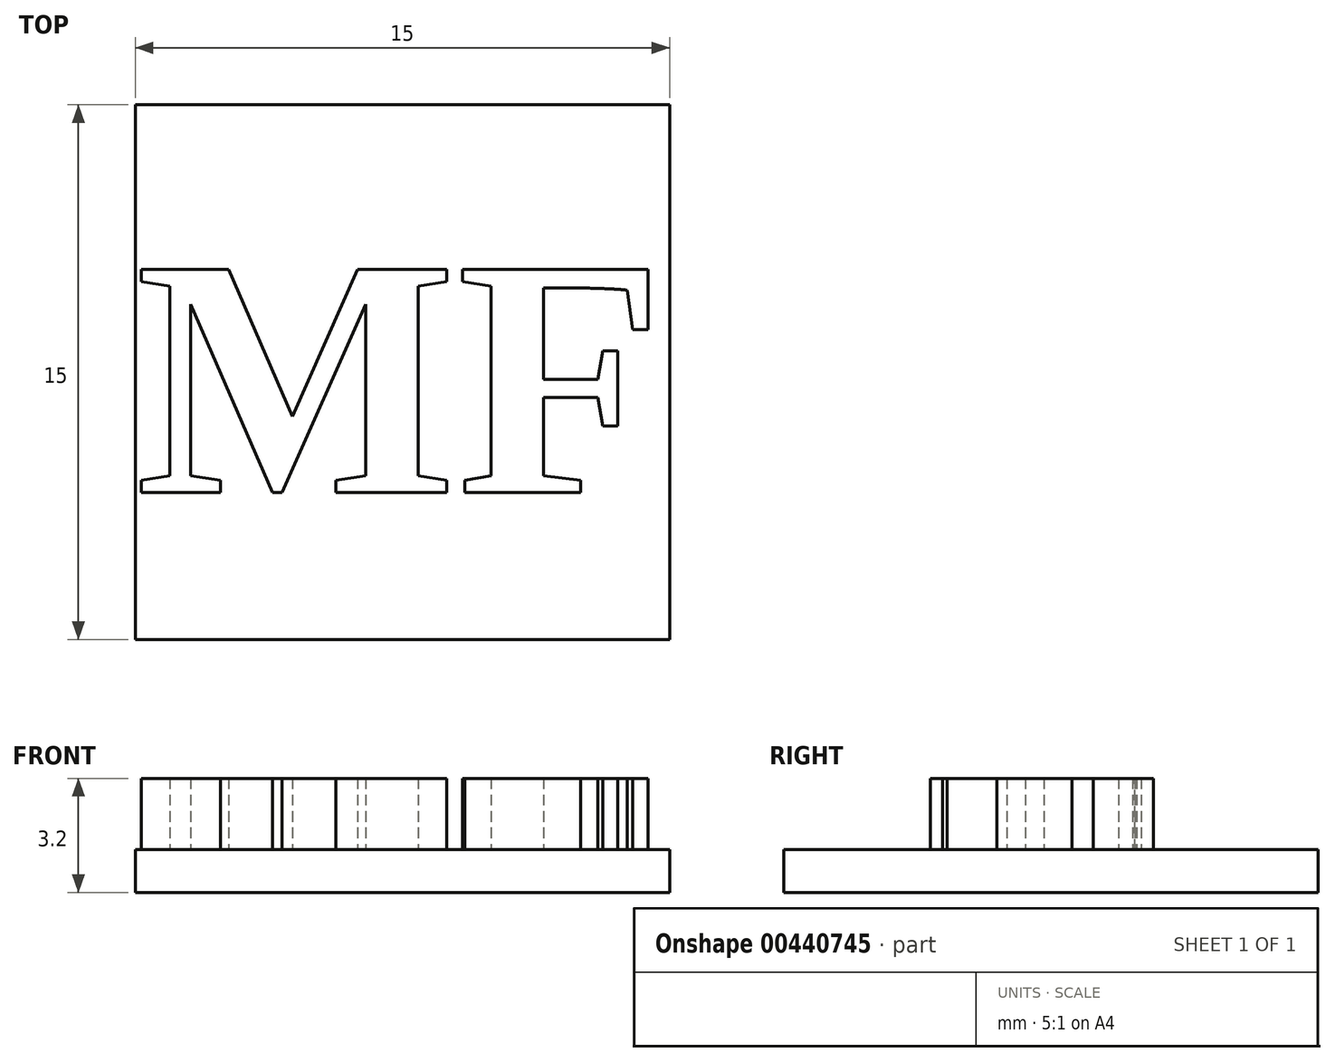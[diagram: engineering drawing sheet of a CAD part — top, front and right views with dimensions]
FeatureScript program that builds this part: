
annotation { "Feature Type Name" : "Feature", "Feature Type Description" : "" }
export const myFeature = defineFeature(function(context is Context, id is Id, definition is map)
    precondition{}
    {
        {
            var Q0;
            Q0=qCreatedBy(makeId("Top.planeOp"),FACE);
            var sketch = newSketch(context, id + "F0", { "sketchPlane" : qUnion([Q0])});
            skLineSegment(sketch, "E0.bottom", {"start": v(0, 0) * mm, "end": v(15, 0) * mm});
            skLineSegment(sketch, "E0.top", {"start": v(0, 15) * mm, "end": v(15, 15) * mm});
            skLineSegment(sketch, "E0.left", {"start": v(0, 0) * mm, "end": v(0, 15) * mm});
            skLineSegment(sketch, "E0.right", {"start": v(15, 0) * mm, "end": v(15, 15) * mm});
            skSolve(sketch);
        }
        {
            var Q0;
            Q0=qSketchRegion(id+"F0",true);
            extrude(context, id + "F1", {"entities" : qUnion([Q0]), "depth" : 1.2 * mm});
        }
        {
            var Q0;
            Q0=makeQuery(id+"F1.opExtrude","CAP_FACE",FACE,{"disambiguationData":[OSD([sQuery(id+"F0.wireOp",EDGE,"E0.bottom"),sQuery(id+"F0.wireOp",EDGE,"E0.top"),sQuery(id+"F0.wireOp",EDGE,"E0.left"),sQuery(id+"F0.wireOp",EDGE,"E0.right")])],"isStart":false});
            var sketch = newSketch(context, id + "F2", { "sketchPlane" : qUnion([Q0])});
            skText(sketch, "E1", { "text": "MF", "fontName": "Tinos-Bold.ttf"});
            const initialGuessF2  = {"E1": [0, 0.00412, 1, 0, 0.00688]};
            skSetInitialGuess(sketch, initialGuessF2);
            skSolve(sketch);
        }
        {
            var Q0;
            Q0 = qSketchRegion(id + "F2", true);
            extrude(context, id + "F3", {"entities" : qUnion([Q0]), "operationType" : NewBodyOperationType.ADD, "depth" : 2 * mm});
        }
    });
